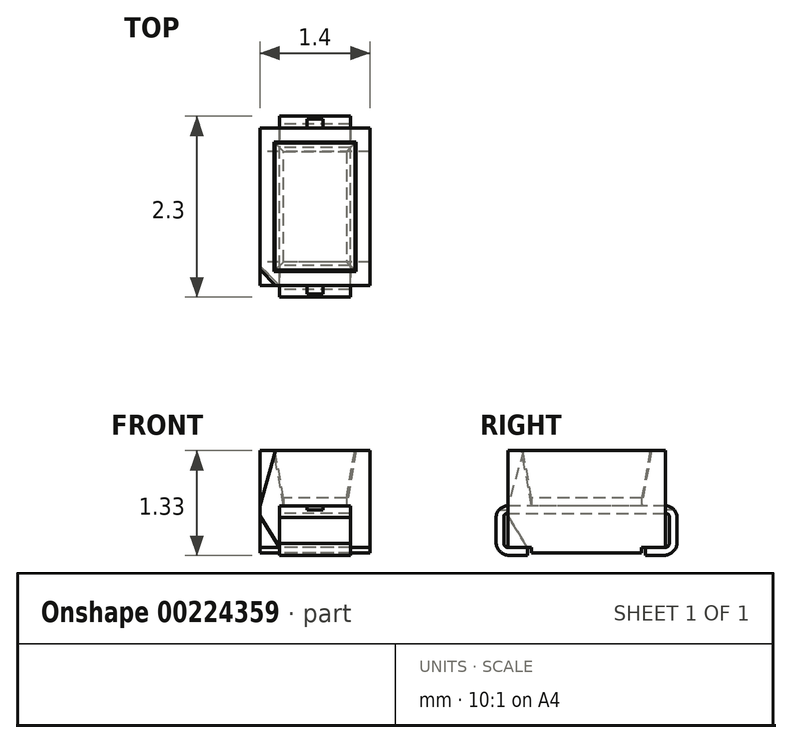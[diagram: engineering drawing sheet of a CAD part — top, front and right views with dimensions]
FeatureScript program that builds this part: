
annotation { "Feature Type Name" : "Feature", "Feature Type Description" : "" }
export const myFeature = defineFeature(function(context is Context, id is Id, definition is map)
    precondition{}
    {
        {
            var Q0;
            Q0=qCreatedBy(makeId("Top.planeOp"),FACE);
            var sketch = newSketch(context, id + "F0", { "sketchPlane" : qUnion([Q0])});
            skLineSegment(sketch, "E0.bottom", {"start": v(0.7, -1) * mm, "end": v(-0.7, -1) * mm});
            skLineSegment(sketch, "E0.top", {"start": v(0.7, 1) * mm, "end": v(-0.7, 1) * mm});
            skLineSegment(sketch, "E0.left", {"start": v(0.7, -1) * mm, "end": v(0.7, 1) * mm});
            skLineSegment(sketch, "E0.right", {"start": v(-0.7, -1) * mm, "end": v(-0.7, 1) * mm});
            skPoint(sketch, "E0.middle", {"position": v(0, 0) * mm});
            skLineSegment(sketch, "E1.bottom", {"start": v(0.4, -0.7) * mm, "end": v(-0.4, -0.7) * mm});
            skLineSegment(sketch, "E1.top", {"start": v(0.4, 0.7) * mm, "end": v(-0.4, 0.7) * mm});
            skLineSegment(sketch, "E1.left", {"start": v(0.4, -0.7) * mm, "end": v(0.4, 0.7) * mm});
            skLineSegment(sketch, "E1.right", {"start": v(-0.4, -0.7) * mm, "end": v(-0.4, 0.7) * mm});
            skLineSegment(sketch, "E2.bottom", {"start": v(0.15, -0.4) * mm, "end": v(-0.15, -0.4) * mm});
            skLineSegment(sketch, "E2.top", {"start": v(0.15, -0.1) * mm, "end": v(-0.15, -0.1) * mm});
            skLineSegment(sketch, "E2.left", {"start": v(0.15, -0.4) * mm, "end": v(0.15, -0.1) * mm});
            skLineSegment(sketch, "E2.right", {"start": v(-0.15, -0.4) * mm, "end": v(-0.15, -0.1) * mm});
            skPoint(sketch, "E2.middle", {"position": v(0, -0.25) * mm});
            skSolve(sketch);
        }
        {
            var Q0;
            Q0=makeQuery(id+"F0.imprint","IMPRINT",FACE,{"disambiguationData":[TD([[makeQuery(id+"F0.imprint","IMPRINT",EDGE,{"derivedFrom":sQuery(id+"F0.wireOp",EDGE,"E0.bottom")}),-1.0]])]});
            var Q1;
            {var subQ1=sQuery(id+"F0.wireOp",EDGE,"E0.top");Q1=makeQuery(id+"F0.imprint","IMPRINT",FACE,{"disambiguationData":[TD([[makeQuery(id+"F0.imprint","IMPRINT",EDGE,{"derivedFrom":subQ1}),1.0]])]});}
            extrude(context, id + "F1", {"entities" : qUnion([Q0, Q1]), "depth" : .7 * mm, "hasSecondDirection" : true, "secondDirectionOppositeDirection" : true, "secondDirectionDepth" : .6 * mm});
        }
        {
            var Q0;
            Q0=makeQuery(id+"F0.imprint","IMPRINT",FACE,{"disambiguationData":[TD([[makeQuery(id+"F0.imprint","IMPRINT",EDGE,{"derivedFrom":sQuery(id+"F0.wireOp",EDGE,"E1.bottom")}),-1.0]])]});
            var Q1;
            Q1=makeQuery(id+"F1.opExtrude","CAP_FACE",FACE,{"disambiguationData":[OSD([sQuery(id+"F0.wireOp",EDGE,"E0.bottom"),sQuery(id+"F0.wireOp",EDGE,"E0.top"),sQuery(id+"F0.wireOp",EDGE,"E0.left"),sQuery(id+"F0.wireOp",EDGE,"E0.right"),sQuery(id+"F0.wireOp",EDGE,"E1.bottom"),sQuery(id+"F0.wireOp",EDGE,"E1.top"),sQuery(id+"F0.wireOp",EDGE,"E1.left"),sQuery(id+"F0.wireOp",EDGE,"E1.right")])],"isStart":false});
            extrude(context, id + "F2", {"entities" : qUnion([Q0]), "operationType" : NewBodyOperationType.REMOVE, "endBound" : BoundingType.UP_TO_SURFACE, "endBoundEntityFace" : qUnion([Q1]), "depth" : 25 * mm, "hasDraft" : true, "draftAngle" : 10 * degree});
        }
        {
            var Q0;
            Q0=makeQuery(id+"F0.imprint","IMPRINT",FACE,{"disambiguationData":[TD([[makeQuery(id+"F0.imprint","IMPRINT",EDGE,{"derivedFrom":sQuery(id+"F0.wireOp",EDGE,"E2.bottom")}),-1.0]])]});
            extrude(context, id + "F3", {"entities" : qUnion([Q0]), "depth" : .1 * mm});
        }
        {
            var Q0;
            Q0=makeQuery(id+"F0.imprint","IMPRINT",FACE,{"disambiguationData":[TD([[makeQuery(id+"F0.imprint","IMPRINT",EDGE,{"derivedFrom":sQuery(id+"F0.wireOp",EDGE,"E1.bottom")}),-1.0]])]});
            var Q1;
            Q1=makeQuery(id+"F1.opExtrude","CAP_FACE",FACE,{"disambiguationData":[OSD([sQuery(id+"F0.wireOp",EDGE,"E0.bottom"),sQuery(id+"F0.wireOp",EDGE,"E0.top"),sQuery(id+"F0.wireOp",EDGE,"E0.left"),sQuery(id+"F0.wireOp",EDGE,"E0.right"),sQuery(id+"F0.wireOp",EDGE,"E1.bottom"),sQuery(id+"F0.wireOp",EDGE,"E1.top"),sQuery(id+"F0.wireOp",EDGE,"E1.left"),sQuery(id+"F0.wireOp",EDGE,"E1.right")])],"isStart":true});
            extrude(context, id + "F4", {"entities" : qUnion([Q0]), "operationType" : NewBodyOperationType.ADD, "endBound" : BoundingType.UP_TO_SURFACE, "oppositeDirection" : true, "endBoundEntityFace" : qUnion([Q1]), "depth" : 25 * mm});
        }
        {
            var Q0;
            Q0=makeQuery(id+"F0.imprint","IMPRINT",FACE,{"disambiguationData":[TD([[makeQuery(id+"F0.imprint","IMPRINT",EDGE,{"derivedFrom":sQuery(id+"F0.wireOp",EDGE,"E1.bottom")}),-1.0]])]});
            extrude(context, id + "F5", {"entities" : qUnion([Q0]), "depth" : .1 * mm});
        }
        {
            var Q0;
            Q0=makeQuery(id+"F0.imprint","IMPRINT",FACE,{"disambiguationData":[TD([[makeQuery(id+"F0.imprint","IMPRINT",EDGE,{"derivedFrom":sQuery(id+"F0.wireOp",EDGE,"E2.bottom")}),-1.0]])]});
            var Q1;
            {var subQ0=sQuery(id+"F0.wireOp",EDGE,"E1.right");var subQ1=sQuery(id+"F0.wireOp",EDGE,"E1.left");var subQ2=sQuery(id+"F0.wireOp",EDGE,"E1.top");var subQ3=sQuery(id+"F0.wireOp",EDGE,"E1.bottom");var subQ4=sQuery(id+"F0.wireOp",EDGE,"E0.right");var subQ5=sQuery(id+"F0.wireOp",EDGE,"E0.left");var subQ6=sQuery(id+"F0.wireOp",EDGE,"E0.top");var subQ7=sQuery(id+"F0.wireOp",EDGE,"E0.bottom");Q1=makeQuery(id+"F4.boolean.opBoolean","MERGE",FACE,{"derivedFrom":[makeQuery(id+"F1.opExtrude","CAP_FACE",FACE,{"disambiguationData":[OSD([subQ7,subQ6,subQ5,subQ4,subQ3,subQ2,subQ1,subQ0])],"isStart":true}),makeQuery(id+"F4.opExtrude","CAP_FACE",FACE,{"disambiguationData":[OSD([subQ7,subQ6,subQ5,subQ4,subQ3,subQ2,subQ1,subQ0])],"isStart":false})]});}
            extrude(context, id + "F6", {"entities" : qUnion([Q0]), "operationType" : NewBodyOperationType.ADD, "endBound" : BoundingType.UP_TO_SURFACE, "oppositeDirection" : true, "endBoundEntityFace" : qUnion([Q1]), "depth" : 25 * mm});
        }
        {
            var Q0;
            Q0=makeQuery(id+"F1.opExtrude","SWEPT_FACE",FACE,{"disambiguationData":[OSD([sQuery(id+"F0.wireOp",EDGE,"E0.right")])]});
            var sketch = newSketch(context, id + "F7", { "sketchPlane" : qUnion([Q0])});
            skLineSegment(sketch, "E3", {"start": v(-1, 0.7) * mm, "end": v(1, 0.7) * mm, "construction": true});
            skLineSegment(sketch, "E4", {"start": v(1, 0.7) * mm, "end": v(1, -0.6) * mm, "construction": true});
            skLineSegment(sketch, "E5", {"start": v(1, -0.6) * mm, "end": v(-1, -0.6) * mm, "construction": true});
            skLineSegment(sketch, "E6", {"start": v(-1, -0.6) * mm, "end": v(-1, 0.7) * mm, "construction": true});
            skLineSegment(sketch, "E7", {"start": v(-1.16, -0.53) * mm, "end": v(-0.7, -0.53) * mm});
            skLineSegment(sketch, "E8", {"start": v(-0.7, -0.53) * mm, "end": v(-0.7, -0.74) * mm});
            skLineSegment(sketch, "E9", {"start": v(-0.7, -0.74) * mm, "end": v(0.7, -0.74) * mm});
            skLineSegment(sketch, "E10", {"start": v(0.7, -0.74) * mm, "end": v(0.7, -0.53) * mm});
            skLineSegment(sketch, "E11", {"start": v(0.7, -0.53) * mm, "end": v(1.16, -0.53) * mm});
            skLineSegment(sketch, "E12", {"start": v(1.16, -0.53) * mm, "end": v(1.16, -0.97) * mm});
            skLineSegment(sketch, "E13", {"start": v(1.16, -0.97) * mm, "end": v(-1.16, -0.97) * mm});
            skLineSegment(sketch, "E14", {"start": v(-1.16, -0.97) * mm, "end": v(-1.16, -0.53) * mm});
            skSolve(sketch);
        }
        {
            var Q0;
            {var subQ0=sQuery(id+"F7.wireOp",EDGE,"E8");var subQ1=sQuery(id+"F7.wireOp",EDGE,"E7");var subQ2=makeQuery(id+"F7.imprint","INTERSECT",VERTEX,{"derivedFrom":[subQ1,subQ0]});Q0=makeQuery(id+"F7.imprint","IMPRINT",FACE,{"disambiguationData":[TD([[makeQuery(id+"F7.imprint","IMPRINT",EDGE,{"disambiguationData":[TD([[subQ2,-1.0]])],"derivedFrom":subQ0}),-1.0]])]});}
            var Q1;
            {var subQ0=sQuery(id+"F7.wireOp",EDGE,"E11");var subQ1=sQuery(id+"F7.wireOp",EDGE,"E10");var subQ2=makeQuery(id+"F7.imprint","INTERSECT",VERTEX,{"derivedFrom":[subQ1,subQ0]});Q1=makeQuery(id+"F7.imprint","IMPRINT",FACE,{"disambiguationData":[TD([[makeQuery(id+"F7.imprint","IMPRINT",EDGE,{"disambiguationData":[TD([[subQ2,1.0]])],"derivedFrom":subQ1}),-1.0]])]});}
            extrude(context, id + "F8", {"entities" : qUnion([Q0, Q1]), "operationType" : NewBodyOperationType.REMOVE, "endBound" : BoundingType.UP_TO_NEXT, "oppositeDirection" : true, "depth" : 25 * mm});
        }
        {
            var Q0;
            Q0=makeQuery(id+"F1.opExtrude","SWEPT_FACE",FACE,{"disambiguationData":[OSD([sQuery(id+"F0.wireOp",EDGE,"E0.right")])]});
            var sketch = newSketch(context, id + "F9", { "sketchPlane" : qUnion([Q0])});
            skLineSegment(sketch, "E15", {"start": v(-1, 0) * mm, "end": v(1, 0) * mm, "construction": true});
            skLineSegment(sketch, "E16", {"start": v(-1.15, -0.15) * mm, "end": v(-1.15, -0.48) * mm});
            skLineSegment(sketch, "E17", {"start": v(-1, -0.63) * mm, "end": v(-0.75, -0.63) * mm});
            skLineSegment(sketch, "E18", {"start": v(-1.15, 0) * mm, "end": v(1.15, 0) * mm});
            skLineSegment(sketch, "E19", {"start": v(1.15, -0.15) * mm, "end": v(1.15, -0.48) * mm});
            skLineSegment(sketch, "E20", {"start": v(1, -0.63) * mm, "end": v(0.75, -0.63) * mm});
            skLineSegment(sketch, "E21", {"start": v(0.75, -0.63) * mm, "end": v(0.75, -0.53) * mm});
            skLineSegment(sketch, "E22", {"start": v(0.75, -0.53) * mm, "end": v(1, -0.53) * mm});
            skLineSegment(sketch, "E23", {"start": v(1.05, -0.48) * mm, "end": v(1.05, -0.15) * mm});
            skLineSegment(sketch, "E24", {"start": v(1, -0.1) * mm, "end": v(-1, -0.1) * mm});
            skLineSegment(sketch, "E25", {"start": v(-1.05, -0.15) * mm, "end": v(-1.05, -0.48) * mm});
            skLineSegment(sketch, "E26", {"start": v(-1, -0.53) * mm, "end": v(-0.75, -0.53) * mm});
            skLineSegment(sketch, "E27", {"start": v(-0.75, -0.53) * mm, "end": v(-0.75, -0.63) * mm});
            skPoint(sketch, "E28.visualSharp", {"position": v(-1.05, -0.1) * mm});
            skArc(sketch, "E28.filletArc", {"start": v(-1, -0.1) * mm, "mid": v(-1.04, -0.11) * mm, "end": v(-1.05, -0.15) * mm});
            skPoint(sketch, "E29.newPointA", {"position": v(0, 0) * mm});
            skArc(sketch, "E29.filletArc", {"start": v(-1, 0) * mm, "mid": v(-1.1, -0.04) * mm, "end": v(-1.15, -0.15) * mm});
            skPoint(sketch, "E30.visualSharp", {"position": v(-1.15, -0.63) * mm});
            skArc(sketch, "E30.filletArc", {"start": v(-1.15, -0.48) * mm, "mid": v(-1.1, -0.58) * mm, "end": v(-1, -0.63) * mm});
            skPoint(sketch, "E31.visualSharp", {"position": v(-1.05, -0.53) * mm});
            skArc(sketch, "E31.filletArc", {"start": v(-1.05, -0.48) * mm, "mid": v(-1.04, -0.51) * mm, "end": v(-1, -0.53) * mm});
            skPoint(sketch, "E32.visualSharp", {"position": v(1.05, -0.53) * mm});
            skArc(sketch, "E32.filletArc", {"start": v(1, -0.53) * mm, "mid": v(1.04, -0.51) * mm, "end": v(1.05, -0.48) * mm});
            skPoint(sketch, "E33.visualSharp", {"position": v(1.05, -0.1) * mm});
            skArc(sketch, "E33.filletArc", {"start": v(1.05, -0.15) * mm, "mid": v(1.04, -0.11) * mm, "end": v(1, -0.1) * mm});
            skArc(sketch, "E34.filletArc", {"start": v(1.15, -0.15) * mm, "mid": v(1.1, -0.04) * mm, "end": v(1, 0) * mm});
            skPoint(sketch, "E35.visualSharp", {"position": v(1.15, -0.63) * mm});
            skArc(sketch, "E35.filletArc", {"start": v(1, -0.63) * mm, "mid": v(1.1, -0.58) * mm, "end": v(1.15, -0.48) * mm});
            skSolve(sketch);
        }
        {
            var Q0;
            Q0=qSketchRegion(id+"F9",true);
            var Q1;
            Q1=makeQuery(id+"F1.opExtrude","SWEPT_FACE",FACE,{"disambiguationData":[OSD([sQuery(id+"F0.wireOp",EDGE,"E0.left")])]});
            extrude(context, id + "F10", {"entities" : qUnion([Q0]), "oppositeDirection" : true, "endBoundEntityFace" : qUnion([Q1]), "depth" : 1.15 * mm, "hasSecondDirection" : true, "secondDirectionOppositeDirection" : true, "secondDirectionDepth" : .25 * mm});
        }
        {
            var Q0;
            Q0=makeQuery(id+"F5.opExtrude","CAP_FACE",FACE,{"disambiguationData":[OSD([sQuery(id+"F0.wireOp",EDGE,"E1.bottom"),sQuery(id+"F0.wireOp",EDGE,"E1.top"),sQuery(id+"F0.wireOp",EDGE,"E1.left"),sQuery(id+"F0.wireOp",EDGE,"E1.right"),sQuery(id+"F0.wireOp",EDGE,"E2.bottom"),sQuery(id+"F0.wireOp",EDGE,"E2.top"),sQuery(id+"F0.wireOp",EDGE,"E2.left"),sQuery(id+"F0.wireOp",EDGE,"E2.right")])],"isStart":false});
            var sketch = newSketch(context, id + "F11", { "sketchPlane" : qUnion([Q0])});
            skLineSegment(sketch, "E36.0.1", {"start": v(-0.45, 1) * mm, "end": v(0.45, 1) * mm});
            skLineSegment(sketch, "E37", {"start": v(0, 1) * mm, "end": v(0.1, 1) * mm});
            skLineSegment(sketch, "E38", {"start": v(0.1, 1) * mm, "end": v(0.1, 1.2) * mm});
            skLineSegment(sketch, "E39", {"start": v(0.1, 1.2) * mm, "end": v(-0.1, 1.2) * mm});
            skLineSegment(sketch, "E40", {"start": v(-0.1, 1.2) * mm, "end": v(-0.1, 1) * mm});
            skLineSegment(sketch, "E41", {"start": v(-0.1, 1) * mm, "end": v(0, 1) * mm});
            skPoint(sketch, "E42.startSnap0", {"position": v(-0.15, -0.25) * mm});
            skPoint(sketch, "E36.0.2.end.orphan", {"position": v(0.45, 1.15) * mm});
            skPoint(sketch, "E36.0.0.start.orphan", {"position": v(-0.45, 1.15) * mm});
            skLineSegment(sketch, "E43", {"start": v(-0.78, 0) * mm, "end": v(1.2, 0) * mm, "construction": true});
            skLineSegment(sketch, "E44.MirrorCS", {"start": v(-0.1, -1) * mm, "end": v(0, -1) * mm});
            skLineSegment(sketch, "E45.MirrorCS", {"start": v(-0.1, -1.2) * mm, "end": v(-0.1, -1) * mm});
            skLineSegment(sketch, "E46.MirrorCS", {"start": v(0, -1) * mm, "end": v(0.1, -1) * mm});
            skLineSegment(sketch, "E47.MirrorCS", {"start": v(0.1, -1.2) * mm, "end": v(-0.1, -1.2) * mm});
            skLineSegment(sketch, "E48.MirrorCS", {"start": v(0.1, -1) * mm, "end": v(0.1, -1.2) * mm});
            skSolve(sketch);
        }
        {
            var Q0;
            Q0=qSketchRegion(id+"F11",true);
            extrude(context, id + "F12", {"entities" : qUnion([Q0]), "operationType" : NewBodyOperationType.REMOVE, "oppositeDirection" : true, "depth" : .15 * mm});
        }
        {
            var Q0;
            Q0=makeQuery(id+"F1.opExtrude","SWEPT_FACE",FACE,{"disambiguationData":[OSD([sQuery(id+"F0.wireOp",EDGE,"E0.bottom")])]});
            var sketch = newSketch(context, id + "F13", { "sketchPlane" : qUnion([Q0])});
            skLineSegment(sketch, "E49", {"start": v(-0.7, 0) * mm, "end": v(-0.5, 0.7) * mm});
            skLineSegment(sketch, "E50", {"start": v(-0.7, -0.13) * mm, "end": v(-0.45, -0.53) * mm});
            skSolve(sketch);
        }
        {
            var Q0;
            Q0=makeQuery(id+"F1.opExtrude","SWEPT_FACE",FACE,{"disambiguationData":[OSD([sQuery(id+"F0.wireOp",EDGE,"E0.right")])]});
            var sketch = newSketch(context, id + "F14", { "sketchPlane" : qUnion([Q0])});
            skLineSegment(sketch, "E51", {"start": v(0.8, 0.7) * mm, "end": v(1, 0) * mm});
            skLineSegment(sketch, "E52", {"start": v(1, 0) * mm, "end": v(1, 0.7) * mm});
            skLineSegment(sketch, "E53", {"start": v(0.7, -0.53) * mm, "end": v(1, -0.53) * mm});
            skLineSegment(sketch, "E54", {"start": v(1, 0.7) * mm, "end": v(1, -0.53) * mm});
            skLineSegment(sketch, "E55", {"start": v(1, 0.7) * mm, "end": v(-1, 0.7) * mm});
            skLineSegment(sketch, "E56", {"start": v(-1, 0.7) * mm, "end": v(-1, -0.53) * mm});
            skLineSegment(sketch, "E57", {"start": v(-1, -0.53) * mm, "end": v(-0.7, -0.53) * mm});
            skLineSegment(sketch, "E58", {"start": v(-0.7, -0.53) * mm, "end": v(-0.7, -0.6) * mm});
            skLineSegment(sketch, "E59", {"start": v(0.7, -0.6) * mm, "end": v(-0.7, -0.6) * mm});
            skLineSegment(sketch, "E60", {"start": v(0.7, -0.6) * mm, "end": v(0.7, -0.53) * mm});
            skLineSegment(sketch, "E61", {"start": v(1, -0.13) * mm, "end": v(0.75, -0.53) * mm});
            skSolve(sketch);
        }
        {
            var Q0;
            Q0=makeQuery(id+"F1.opExtrude","CAP_FACE",FACE,{"disambiguationData":[OSD([sQuery(id+"F0.wireOp",EDGE,"E0.bottom"),sQuery(id+"F0.wireOp",EDGE,"E0.top"),sQuery(id+"F0.wireOp",EDGE,"E0.left"),sQuery(id+"F0.wireOp",EDGE,"E0.right"),sQuery(id+"F0.wireOp",EDGE,"E1.bottom"),sQuery(id+"F0.wireOp",EDGE,"E1.top"),sQuery(id+"F0.wireOp",EDGE,"E1.left"),sQuery(id+"F0.wireOp",EDGE,"E1.right")])],"isStart":false});
            var sketch = newSketch(context, id + "F15", { "sketchPlane" : qUnion([Q0])});
            skLineSegment(sketch, "E62", {"start": v(-0.7, -0.8) * mm, "end": v(-0.5, -1) * mm});
            skSolve(sketch);
        }
        {
            var Q0;
            Q0=sQuery(id+"F15.wireOp",VERTEX,"E62.start");
            var Q1;
            Q1=sQuery(id+"F15.wireOp",VERTEX,"E62.end");
            var Q2;
            Q2=sQuery(id+"F14.wireOp",VERTEX,"E52.start");
            cPlane(context, id + "F16", {"entities" : qUnion([Q0, Q1, Q2]), "cplaneType" : CPlaneType.THREE_POINT, "offset" : 25 * mm, "width" : 150 * mm, "height" : 150 * mm});
        }
        {
            var Q0;
            Q0=qCreatedBy(id+"F16.planeOp",FACE);
            var sketch = newSketch(context, id + "F17", { "sketchPlane" : qUnion([Q0])});
            skLineSegment(sketch, "E63.bottom", {"start": v(-0.04, 0.54) * mm, "end": v(0.57, 0.54) * mm});
            skLineSegment(sketch, "E63.top", {"start": v(-0.04, -0.39) * mm, "end": v(0.57, -0.39) * mm});
            skLineSegment(sketch, "E63.left", {"start": v(-0.04, 0.54) * mm, "end": v(-0.04, -0.39) * mm});
            skLineSegment(sketch, "E63.right", {"start": v(0.57, 0.54) * mm, "end": v(0.57, -0.39) * mm});
            skSolve(sketch);
        }
        {
            var Q0;
            Q0=qSketchRegion(id+"F17",true);
            extrude(context, id + "F18", {"entities" : qUnion([Q0]), "operationType" : NewBodyOperationType.REMOVE, "endBound" : BoundingType.UP_TO_NEXT, "depth" : 25 * mm});
        }
        {
            var Q0;
            Q0=makeQuery(id+"F8.boolean.opBoolean","COPY",FACE,{"derivedFrom":makeQuery(id+"F8.opExtrude","SWEPT_FACE",FACE,{"disambiguationData":[OSD([sQuery(id+"F7.wireOp",EDGE,"E11")])]})});
            var sketch = newSketch(context, id + "F19", { "sketchPlane" : qUnion([Q0])});
            skLineSegment(sketch, "E64", {"start": v(-0.7, 0.75) * mm, "end": v(-0.45, 1) * mm});
            skSolve(sketch);
        }
        {
            var Q0;
            Q0=sQuery(id+"F19.wireOp",VERTEX,"E64.start");
            var Q1;
            Q1=sQuery(id+"F13.wireOp",VERTEX,"E50.end");
            var Q2;
            Q2=sQuery(id+"F14.wireOp",VERTEX,"E61.start");
            cPlane(context, id + "F20", {"entities" : qUnion([Q0, Q1, Q2]), "cplaneType" : CPlaneType.THREE_POINT, "offset" : 25 * mm, "width" : 150 * mm, "height" : 150 * mm});
        }
        {
            var Q0;
            Q0=qCreatedBy(id+"F20.planeOp",FACE);
            var sketch = newSketch(context, id + "F21", { "sketchPlane" : qUnion([Q0])});
            skLineSegment(sketch, "E65.0", {"start": v(-0.06, 0.42) * mm, "end": v(-0.06, -0.05) * mm});
            skLineSegment(sketch, "E65.1", {"start": v(-0.06, -0.05) * mm, "end": v(-0.39, 0.08) * mm});
            skLineSegment(sketch, "E65.2", {"start": v(-0.06, 0.42) * mm, "end": v(-0.39, 0.08) * mm});
            skSolve(sketch);
        }
        {
            var Q0;
            Q0 = qSketchRegion(id + "F21", true);
            extrude(context, id + "F22", {"entities" : qUnion([Q0]), "operationType" : NewBodyOperationType.REMOVE, "endBound" : BoundingType.THROUGH_ALL, "oppositeDirection" : true, "depth" : 25 * mm});
        }
        {
            var Q0;
            Q0=makeQuery(id+"F5.opExtrude","CAP_FACE",FACE,{"disambiguationData":[OSD([sQuery(id+"F0.wireOp",EDGE,"E1.bottom"),sQuery(id+"F0.wireOp",EDGE,"E1.top"),sQuery(id+"F0.wireOp",EDGE,"E1.left"),sQuery(id+"F0.wireOp",EDGE,"E1.right"),sQuery(id+"F0.wireOp",EDGE,"E2.bottom"),sQuery(id+"F0.wireOp",EDGE,"E2.top"),sQuery(id+"F0.wireOp",EDGE,"E2.left"),sQuery(id+"F0.wireOp",EDGE,"E2.right")])],"isStart":false});
            var sketch = newSketch(context, id + "F23", { "sketchPlane" : qUnion([Q0])});
            skLineSegment(sketch, "E66", {"start": v(-0.4, 0.7) * mm, "end": v(0.4, 0.7) * mm});
            skLineSegment(sketch, "E67", {"start": v(0.4, 0.7) * mm, "end": v(0.4, -0.7) * mm});
            skLineSegment(sketch, "E68", {"start": v(0.4, -0.7) * mm, "end": v(-0.4, -0.7) * mm});
            skLineSegment(sketch, "E69", {"start": v(-0.4, -0.7) * mm, "end": v(-0.4, 0.7) * mm});
            skSolve(sketch);
        }
        {
            var Q0;
            Q0 = qSketchRegion(id + "F23", true);
            var Q1;
            Q1=makeQuery(id+"F1.opExtrude","CAP_FACE",FACE,{"disambiguationData":[OSD([sQuery(id+"F0.wireOp",EDGE,"E0.bottom"),sQuery(id+"F0.wireOp",EDGE,"E0.top"),sQuery(id+"F0.wireOp",EDGE,"E0.left"),sQuery(id+"F0.wireOp",EDGE,"E0.right"),sQuery(id+"F0.wireOp",EDGE,"E1.bottom"),sQuery(id+"F0.wireOp",EDGE,"E1.top"),sQuery(id+"F0.wireOp",EDGE,"E1.left"),sQuery(id+"F0.wireOp",EDGE,"E1.right")])],"isStart":false});
            extrude(context, id + "F24", {"entities" : qUnion([Q0]), "endBound" : BoundingType.UP_TO_SURFACE, "endBoundEntityFace" : qUnion([Q1]), "depth" : 25 * mm, "hasDraft" : true, "draftAngle" : 10 * degree});
        }
    });
